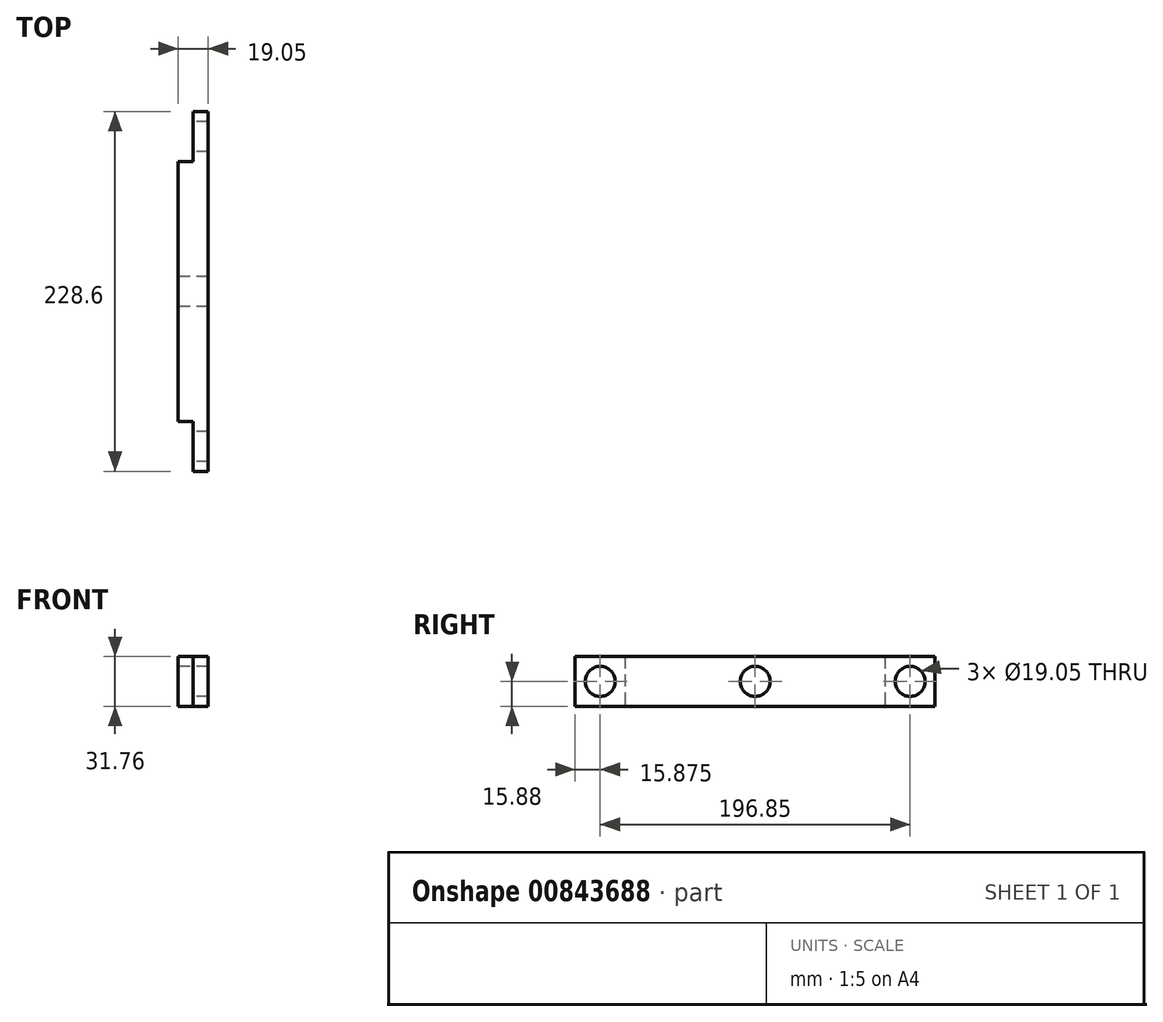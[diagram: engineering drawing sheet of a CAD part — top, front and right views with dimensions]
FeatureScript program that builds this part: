
annotation { "Feature Type Name" : "Feature", "Feature Type Description" : "" }
export const myFeature = defineFeature(function(context is Context, id is Id, definition is map)
    precondition{}
    {
        {
            var Q0;
            Q0=qCreatedBy(makeId("Right.planeOp"),FACE);
            var sketch = newSketch(context, id + "F0", { "sketchPlane" : qUnion([Q0])});
            skLineSegment(sketch, "E0.bottom", {"start": v(114.3, 15.88) * mm, "end": v(-114.3, 15.88) * mm});
            skLineSegment(sketch, "E0.top", {"start": v(114.3, -15.87) * mm, "end": v(-114.3, -15.87) * mm});
            skLineSegment(sketch, "E0.left", {"start": v(114.3, 15.88) * mm, "end": v(114.3, -15.87) * mm});
            skLineSegment(sketch, "E0.right", {"start": v(-114.3, 15.88) * mm, "end": v(-114.3, -15.87) * mm});
            skPoint(sketch, "E0.middle", {"position": v(0, 0) * mm});
            skSolve(sketch);
        }
        {
            var Q0;
            Q0 = qSketchRegion(id + "F0", true);
            extrude(context, id + "F1", {"entities" : qUnion([Q0]), "depth" : 19.05 * mm, "offsetDistance" : 25.4 * mm});
        }
        {
            var Q0;
            Q0=makeQuery(id+"F1.opExtrude","CAP_FACE",FACE,{"disambiguationData":[OSD([sQuery(id+"F0.wireOp",EDGE,"E0.bottom"),sQuery(id+"F0.wireOp",EDGE,"E0.top"),sQuery(id+"F0.wireOp",EDGE,"E0.left"),sQuery(id+"F0.wireOp",EDGE,"E0.right")])],"isStart":true});
            var sketch = newSketch(context, id + "F2", { "sketchPlane" : qUnion([Q0])});
            skLineSegment(sketch, "E1.bottom", {"start": v(-114.3, 15.88) * mm, "end": v(-82.55, 15.88) * mm});
            skLineSegment(sketch, "E1.top", {"start": v(-114.3, -15.87) * mm, "end": v(-82.55, -15.87) * mm});
            skLineSegment(sketch, "E1.left", {"start": v(-114.3, 15.88) * mm, "end": v(-114.3, -15.88) * mm});
            skLineSegment(sketch, "E1.right", {"start": v(-82.55, 15.88) * mm, "end": v(-82.55, -15.88) * mm});
            skLineSegment(sketch, "E2.MirrorCS", {"start": v(82.55, 15.88) * mm, "end": v(82.55, -15.88) * mm});
            skLineSegment(sketch, "E3.MirrorCS", {"start": v(114.3, 15.88) * mm, "end": v(82.55, 15.88) * mm});
            skLineSegment(sketch, "E4.MirrorCS", {"start": v(114.3, -15.87) * mm, "end": v(82.55, -15.87) * mm});
            skLineSegment(sketch, "E5.MirrorCS", {"start": v(114.3, 15.88) * mm, "end": v(114.3, -15.88) * mm});
            skSolve(sketch);
        }
        {
            var Q0;
            Q0 = qSketchRegion(id + "F2", true);
            extrude(context, id + "F3", {"entities" : qUnion([Q0]), "operationType" : NewBodyOperationType.REMOVE, "oppositeDirection" : true, "depth" : 9.52 * mm, "offsetDistance" : 25.4 * mm});
        }
        {
            var Q0;
            Q0=makeQuery(id+"F3.boolean.opBoolean","COPY",FACE,{"derivedFrom":makeQuery(id+"F3.opExtrude","CAP_FACE",FACE,{"disambiguationData":[OSD([sQuery(id+"F2.wireOp",EDGE,"E1.bottom"),sQuery(id+"F2.wireOp",EDGE,"E1.top"),sQuery(id+"F2.wireOp",EDGE,"E1.left"),sQuery(id+"F2.wireOp",EDGE,"E1.right")])],"isStart":false})});
            var sketch = newSketch(context, id + "F4", { "sketchPlane" : qUnion([Q0])});
            skLineSegment(sketch, "E6", {"start": v(-114.3, -15.88) * mm, "end": v(-82.55, 15.88) * mm});
            skCircle(sketch, "E7", {"center": v(-98.42, 0) * mm, "radius": 9.53 * mm});
            skCircle(sketch, "E8.MirrorC", {"center": v(98.42, 0) * mm, "radius": 9.53 * mm});
            skSolve(sketch);
        }
        {
            var Q0;
            Q0 = qSketchRegion(id + "F4", true);
            extrude(context, id + "F5", {"entities" : qUnion([Q0]), "operationType" : NewBodyOperationType.REMOVE, "oppositeDirection" : true, "depth" : 25.4 * mm, "offsetDistance" : 25.4 * mm});
        }
        {
            var Q0;
            Q0=makeQuery(id+"F1.opExtrude","CAP_FACE",FACE,{"disambiguationData":[OSD([sQuery(id+"F0.wireOp",EDGE,"E0.bottom"),sQuery(id+"F0.wireOp",EDGE,"E0.top"),sQuery(id+"F0.wireOp",EDGE,"E0.left"),sQuery(id+"F0.wireOp",EDGE,"E0.right")])],"isStart":true});
            var sketch = newSketch(context, id + "F6", { "sketchPlane" : qUnion([Q0])});
            skCircle(sketch, "E9", {"center": v(0, 0) * mm, "radius": 9.53 * mm});
            skSolve(sketch);
        }
        {
            var Q0;
            Q0 = qSketchRegion(id + "F6", true);
            extrude(context, id + "F7", {"entities" : qUnion([Q0]), "operationType" : NewBodyOperationType.REMOVE, "oppositeDirection" : true, "depth" : 25.4 * mm, "offsetDistance" : 25.4 * mm});
        }
    });
